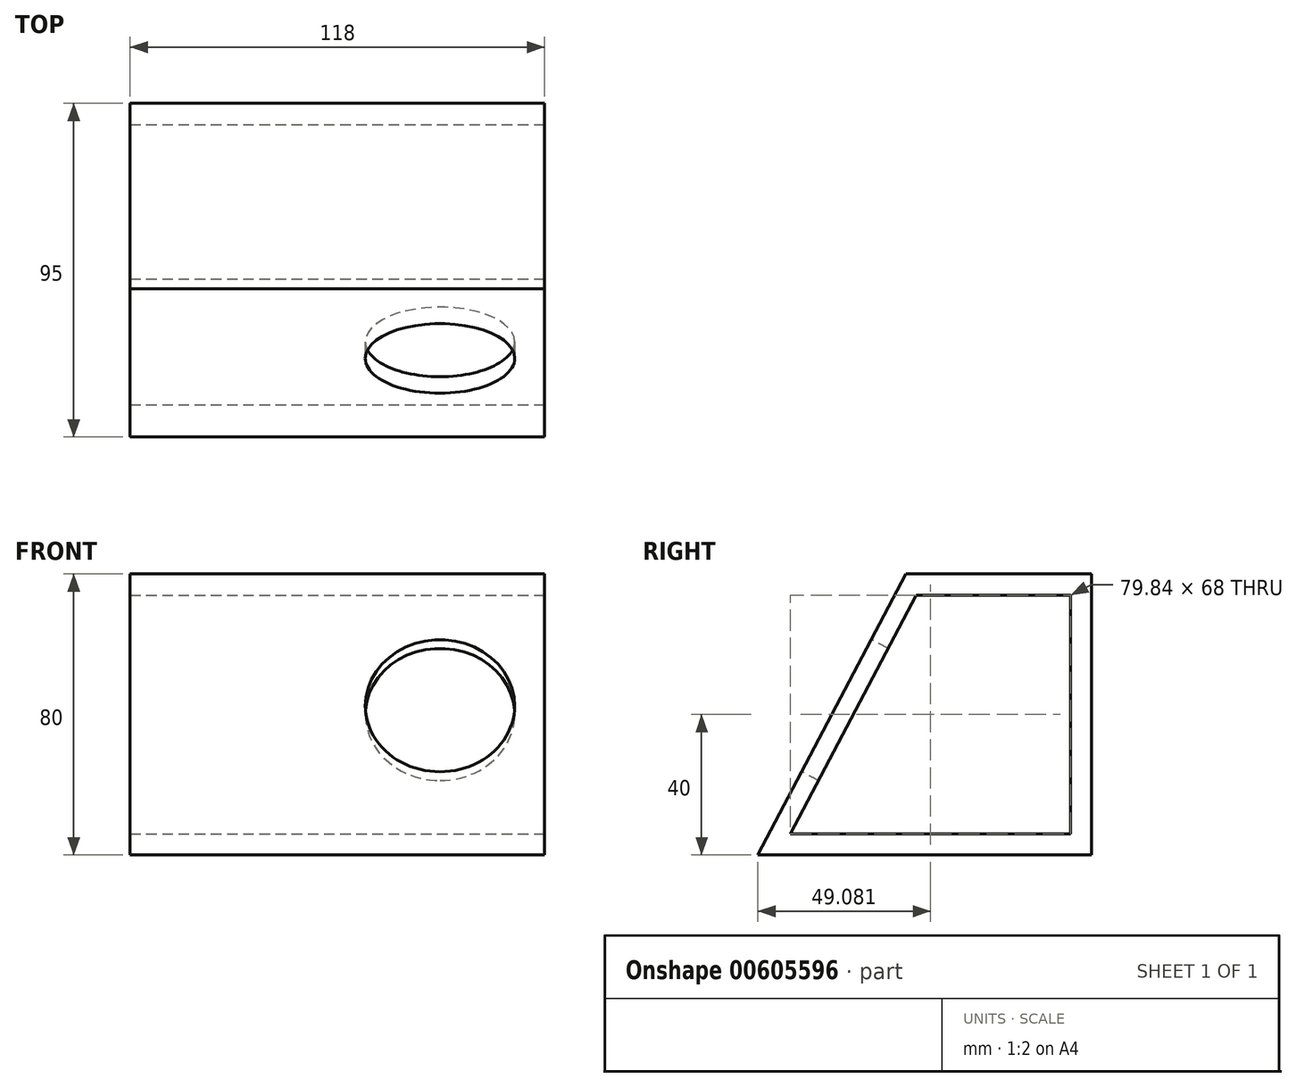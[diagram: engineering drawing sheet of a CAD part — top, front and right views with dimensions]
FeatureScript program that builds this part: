
annotation { "Feature Type Name" : "Feature", "Feature Type Description" : "" }
export const myFeature = defineFeature(function(context is Context, id is Id, definition is map)
    precondition{}
    {
        {
            var Q0;
            Q0=qCreatedBy(makeId("Top.planeOp"),FACE);
            var sketch = newSketch(context, id + "F0", { "sketchPlane" : qUnion([Q0])});
            skLineSegment(sketch, "E0.bottom", {"start": v(-59, 47.5) * mm, "end": v(59, 47.5) * mm});
            skLineSegment(sketch, "E0.top", {"start": v(-59, -47.5) * mm, "end": v(59, -47.5) * mm});
            skLineSegment(sketch, "E0.left", {"start": v(-59, 47.5) * mm, "end": v(-59, -47.5) * mm});
            skLineSegment(sketch, "E0.right", {"start": v(59, 47.5) * mm, "end": v(59, -47.5) * mm});
            skPoint(sketch, "E0.middle", {"position": v(0, 0) * mm});
            skSolve(sketch);
        }
        {
            var Q0;
            Q0=makeQuery(id+"F0.imprint","IMPRINT",FACE,{"disambiguationData":[TD([[makeQuery(id+"F0.imprint","IMPRINT",EDGE,{"derivedFrom":sQuery(id+"F0.wireOp",EDGE,"E0.bottom")}),-1.0]])]});
            extrude(context, id + "F1", {"entities" : qUnion([Q0]), "depth" : 6 * mm, "offsetDistance" : 25 * mm});
        }
        {
            var Q0;
            Q0=makeQuery(id+"F1.opExtrude","SWEPT_FACE",FACE,{"disambiguationData":[OSD([sQuery(id+"F0.wireOp",EDGE,"E0.bottom")])]});
            var sketch = newSketch(context, id + "F2", { "sketchPlane" : qUnion([Q0])});
            skLineSegment(sketch, "E1.bottom", {"start": v(-59, 0) * mm, "end": v(59, 0) * mm});
            skLineSegment(sketch, "E1.top", {"start": v(-59, 80) * mm, "end": v(59, 80) * mm});
            skLineSegment(sketch, "E1.left", {"start": v(-59, 0) * mm, "end": v(-59, 80) * mm});
            skLineSegment(sketch, "E1.right", {"start": v(59, 0) * mm, "end": v(59, 80) * mm});
            skSolve(sketch);
        }
        {
            var Q0;
            {var subQ0=sQuery(id+"F2.wireOp",EDGE,"E1.top");Q0=makeQuery(id+"F2.imprint","IMPRINT",FACE,{"disambiguationData":[TD([[makeQuery(id+"F2.imprint","IMPRINT",EDGE,{"derivedFrom":subQ0}),-1.0]])]});}
            extrude(context, id + "F3", {"entities" : qUnion([Q0]), "operationType" : NewBodyOperationType.ADD, "oppositeDirection" : true, "depth" : 6 * mm, "offsetDistance" : 25 * mm});
        }
        {
            var Q0;
            Q0=makeQuery(id+"F3.opExtrude","CAP_FACE",FACE,{"disambiguationData":[OSD([sQuery(id+"F0.wireOp",EDGE,"E0.bottom"),sQuery(id+"F2.wireOp",EDGE,"E1.top"),sQuery(id+"F2.wireOp",EDGE,"E1.left"),sQuery(id+"F2.wireOp",EDGE,"E1.right")])],"isStart":false});
            var sketch = newSketch(context, id + "F4", { "sketchPlane" : qUnion([Q0])});
            skLineSegment(sketch, "E2.bottom", {"start": v(-59, 80) * mm, "end": v(59, 80) * mm});
            skLineSegment(sketch, "E2.top", {"start": v(-59, 74) * mm, "end": v(59, 74) * mm});
            skLineSegment(sketch, "E2.left", {"start": v(-59, 80) * mm, "end": v(-59, 74) * mm});
            skLineSegment(sketch, "E2.right", {"start": v(59, 80) * mm, "end": v(59, 74) * mm});
            skSolve(sketch);
        }
        {
            var Q0;
            Q0=makeQuery(id+"F4.imprint","IMPRINT",FACE,{"disambiguationData":[TD([[makeQuery(id+"F4.imprint","IMPRINT",EDGE,{"derivedFrom":sQuery(id+"F4.wireOp",EDGE,"E2.bottom")}),1.0]])]});
            extrude(context, id + "F5", {"entities" : qUnion([Q0]), "operationType" : NewBodyOperationType.ADD, "depth" : 50 * mm, "offsetDistance" : 25 * mm});
        }
        {
            var Q0;
            Q0=makeQuery(id+"F5.boolean.opBoolean","MERGE",FACE,{"derivedFrom":[makeQuery(id+"F3.boolean.opBoolean","MERGE",FACE,{"derivedFrom":[makeQuery(id+"F1.opExtrude","SWEPT_FACE",FACE,{"disambiguationData":[OSD([sQuery(id+"F0.wireOp",EDGE,"E0.left")])]}),makeQuery(id+"F3.opExtrude","SWEPT_FACE",FACE,{"disambiguationData":[OSD([sQuery(id+"F2.wireOp",EDGE,"E1.right")])]})]}),makeQuery(id+"F5.opExtrude","SWEPT_FACE",FACE,{"disambiguationData":[OSD([sQuery(id+"F4.wireOp",EDGE,"E2.left")])]})]});
            var sketch = newSketch(context, id + "F6", { "sketchPlane" : qUnion([Q0])});
            skLineSegment(sketch, "E3", {"start": v(47.5, 0) * mm, "end": v(41.5, 0) * mm});
            skLineSegment(sketch, "E4", {"start": v(41.5, 0) * mm, "end": v(-0.66, 80) * mm});
            skLineSegment(sketch, "E5", {"start": v(5.34, 80) * mm, "end": v(-0.66, 80) * mm});
            skLineSegment(sketch, "E6", {"start": v(5.34, 80) * mm, "end": v(47.5, 0) * mm});
            skSolve(sketch);
        }
        {
            var Q0;
            {var subQ1=makeQuery(id+"F1.opExtrude","CAP_EDGE",EDGE,{"disambiguationData":[OSD([sQuery(id+"F0.wireOp",EDGE,"E0.left")])],"isStart":false});var subQ6=sQuery(id+"F6.wireOp",EDGE,"E6");var subQ8=makeQuery(id+"F6.imprint","INTERSECT",VERTEX,{"derivedFrom":[subQ1,subQ6]});Q0=makeQuery(id+"F6.imprint","IMPRINT",FACE,{"disambiguationData":[TD([[makeQuery(id+"F6.imprint","IMPRINT",EDGE,{"disambiguationData":[TD([[subQ8,1.0]])],"derivedFrom":subQ1}),1.0]])]});}
            var Q1;
            {var subQ0=sQuery(id+"F6.wireOp",EDGE,"E5");Q1=makeQuery(id+"F6.imprint","IMPRINT",FACE,{"disambiguationData":[TD([[makeQuery(id+"F6.imprint","IMPRINT",EDGE,{"derivedFrom":subQ0}),1.0]])]});}
            var Q2;
            {var subQ0=sQuery(id+"F6.wireOp",EDGE,"E3");Q2=makeQuery(id+"F6.imprint","IMPRINT",FACE,{"disambiguationData":[TD([[makeQuery(id+"F6.imprint","IMPRINT",EDGE,{"derivedFrom":subQ0}),1.0]])]});}
            extrude(context, id + "F7", {"entities" : qUnion([Q0, Q1, Q2]), "operationType" : NewBodyOperationType.ADD, "oppositeDirection" : true, "depth" : 118 * mm, "offsetDistance" : 25 * mm});
        }
        {
            var Q0;
            Q0=makeQuery(id+"F7.boolean.opBoolean","MERGE",FACE,{"derivedFrom":[makeQuery(id+"F5.boolean.opBoolean","MERGE",FACE,{"derivedFrom":[makeQuery(id+"F3.boolean.opBoolean","MERGE",FACE,{"derivedFrom":[makeQuery(id+"F1.opExtrude","SWEPT_FACE",FACE,{"disambiguationData":[OSD([sQuery(id+"F0.wireOp",EDGE,"E0.right")])]}),makeQuery(id+"F3.opExtrude","SWEPT_FACE",FACE,{"disambiguationData":[OSD([sQuery(id+"F2.wireOp",EDGE,"E1.left")])]})]}),makeQuery(id+"F5.opExtrude","SWEPT_FACE",FACE,{"disambiguationData":[OSD([sQuery(id+"F4.wireOp",EDGE,"E2.right")])]})]}),makeQuery(id+"F7.opExtrude","CAP_FACE",FACE,{"disambiguationData":[OSD([sQuery(id+"F6.wireOp",EDGE,"E3"),sQuery(id+"F6.wireOp",EDGE,"E4"),sQuery(id+"F6.wireOp",EDGE,"E5"),sQuery(id+"F6.wireOp",EDGE,"E6")])],"isStart":false})]});
            var sketch = newSketch(context, id + "F8", { "sketchPlane" : qUnion([Q0])});
            skLineSegment(sketch, "E7", {"start": v(-47.5, 0) * mm, "end": v(-5.34, 80) * mm});
            skLineSegment(sketch, "E8", {"start": v(-5.34, 80) * mm, "end": v(-8.5, 80) * mm});
            skLineSegment(sketch, "E9", {"start": v(-8.5, 80) * mm, "end": v(-8.5, 74) * mm});
            skLineSegment(sketch, "E10", {"start": v(-8.5, 74) * mm, "end": v(-44.34, 6) * mm});
            skLineSegment(sketch, "E11", {"start": v(-44.34, 6) * mm, "end": v(-47.5, 6) * mm});
            skLineSegment(sketch, "E12", {"start": v(-47.5, 6) * mm, "end": v(-47.5, 0) * mm});
            skSolve(sketch);
        }
        {
            var Q0;
            Q0 = qSketchRegion(id + "F8", true);
            extrude(context, id + "F9", {"entities" : qUnion([Q0]), "operationType" : NewBodyOperationType.REMOVE, "endBound" : BoundingType.THROUGH_ALL, "oppositeDirection" : true, "depth" : 25 * mm, "offsetDistance" : 25 * mm});
        }
        {
            var Q0;
            {var subQ0=sQuery(id+"F8.wireOp",EDGE,"E10");var subQ1=sQuery(id+"F8.wireOp",EDGE,"E7");Q0=makeQuery(id+"F9.boolean.opBoolean","MERGE",FACE,{"derivedFrom":[makeQuery(id+"F7.opExtrude","SWEPT_FACE",FACE,{"disambiguationData":[OSD([sQuery(id+"F6.wireOp",EDGE,"E6")])]}),makeQuery(id+"F9.opExtrude","SWEPT_FACE",FACE,{"disambiguationData":[OSD([subQ1]),TDD([makeQuery(id+"F8.imprint","IMPRINT",EDGE,{"disambiguationData":[TD([[makeQuery(id+"F8.imprint","INTERSECT",VERTEX,{"derivedFrom":[makeQuery(id+"F1.opExtrude","CAP_EDGE",EDGE,{"disambiguationData":[OSD([sQuery(id+"F0.wireOp",EDGE,"E0.right")])],"isStart":true}),subQ1,sQuery(id+"F8.wireOp",EDGE,"E12")]}),-1.0]])],"derivedFrom":subQ1})])]}),makeQuery(id+"F9.opExtrude","SWEPT_FACE",FACE,{"disambiguationData":[OSD([subQ1]),TDD([makeQuery(id+"F8.imprint","IMPRINT",EDGE,{"disambiguationData":[TD([[makeQuery(id+"F8.imprint","INTERSECT",VERTEX,{"derivedFrom":[subQ1,sQuery(id+"F8.wireOp",EDGE,"E9"),subQ0]}),-1.0]])],"derivedFrom":subQ1})])]})]});}
            var sketch = newSketch(context, id + "F10", { "sketchPlane" : qUnion([Q0])});
            skLineSegment(sketch, "E13", {"start": v(0, -22.15) * mm, "end": v(0, 68.28) * mm});
            skSolve(sketch);
        }
        {
            var Q0;
            {var subQ0=sQuery(id+"F10.wireOp",EDGE,"E13");Q0=makeQuery(id+"F10.imprint","IMPRINT",FACE,{"disambiguationData":[TD([[makeQuery(id+"F10.imprint","IMPRINT",EDGE,{"derivedFrom":subQ0}),-1.0]])]});}
            var sketch = newSketch(context, id + "F11", { "sketchPlane" : qUnion([Q0])});
            skCircle(sketch, "E14", {"center": v(29.21, 25.9) * mm, "radius": 21.25 * mm});
            skCircle(sketch, "E15.MirrorC", {"center": v(-29.21, 25.9) * mm, "radius": 21.25 * mm});
            skSolve(sketch);
        }
        {
            var Q0;
            Q0=makeQuery(id+"F11.imprint","IMPRINT",FACE,{"disambiguationData":[TD([[makeQuery(id+"F11.imprint","IMPRINT",EDGE,{"derivedFrom":sQuery(id+"F11.wireOp",EDGE,"E15.MirrorC")}),-1.0]])]});
            var Q1;
            Q1=makeQuery(id+"F11.imprint","IMPRINT",FACE,{"disambiguationData":[TD([[makeQuery(id+"F11.imprint","IMPRINT",EDGE,{"derivedFrom":sQuery(id+"F11.wireOp",EDGE,"E14")}),1.0]])]});
            extrude(context, id + "F12", {"entities" : qUnion([Q0, Q1]), "operationType" : NewBodyOperationType.REMOVE, "endBound" : BoundingType.UP_TO_NEXT, "oppositeDirection" : true, "depth" : 25 * mm, "offsetDistance" : 25 * mm});
        }
    });
